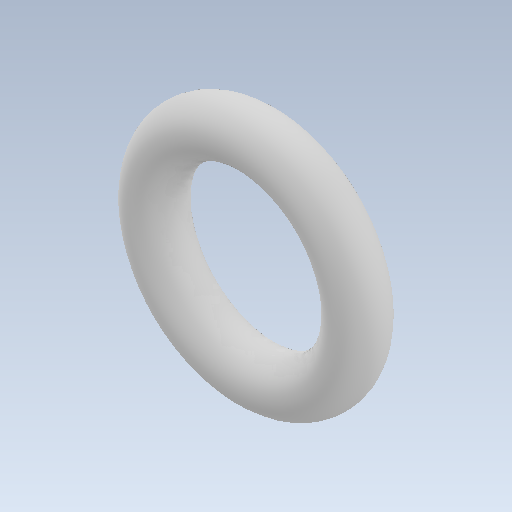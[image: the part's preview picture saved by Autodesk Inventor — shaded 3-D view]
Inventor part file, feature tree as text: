
AUTODESK INVENTOR PART (.ipt)
format: ipt  version: 2021 (Build 250183000, 183)  size: 156,672 bytes
history: native  units: mm
features: revolve x1, sketch x1
ambient origin geometry x8: Origin, YZ Plane, XZ Plane, XY Plane, X Axis, Y Axis, Z Axis, Center Point
bodies: Solid1 (feature_tree)
feature tree (2):
  revolve  "Revolution1"  [1 undecoded]
  sketch  "Sketch1"  dims[d0=7.06mm d1=1.78mm d2=90.0deg]
note: 1 required parameter value undecoded (feature->parameter linkage not recoverable at this tier; creation-order binding heuristic only, values carry confidence <= 0.55)
